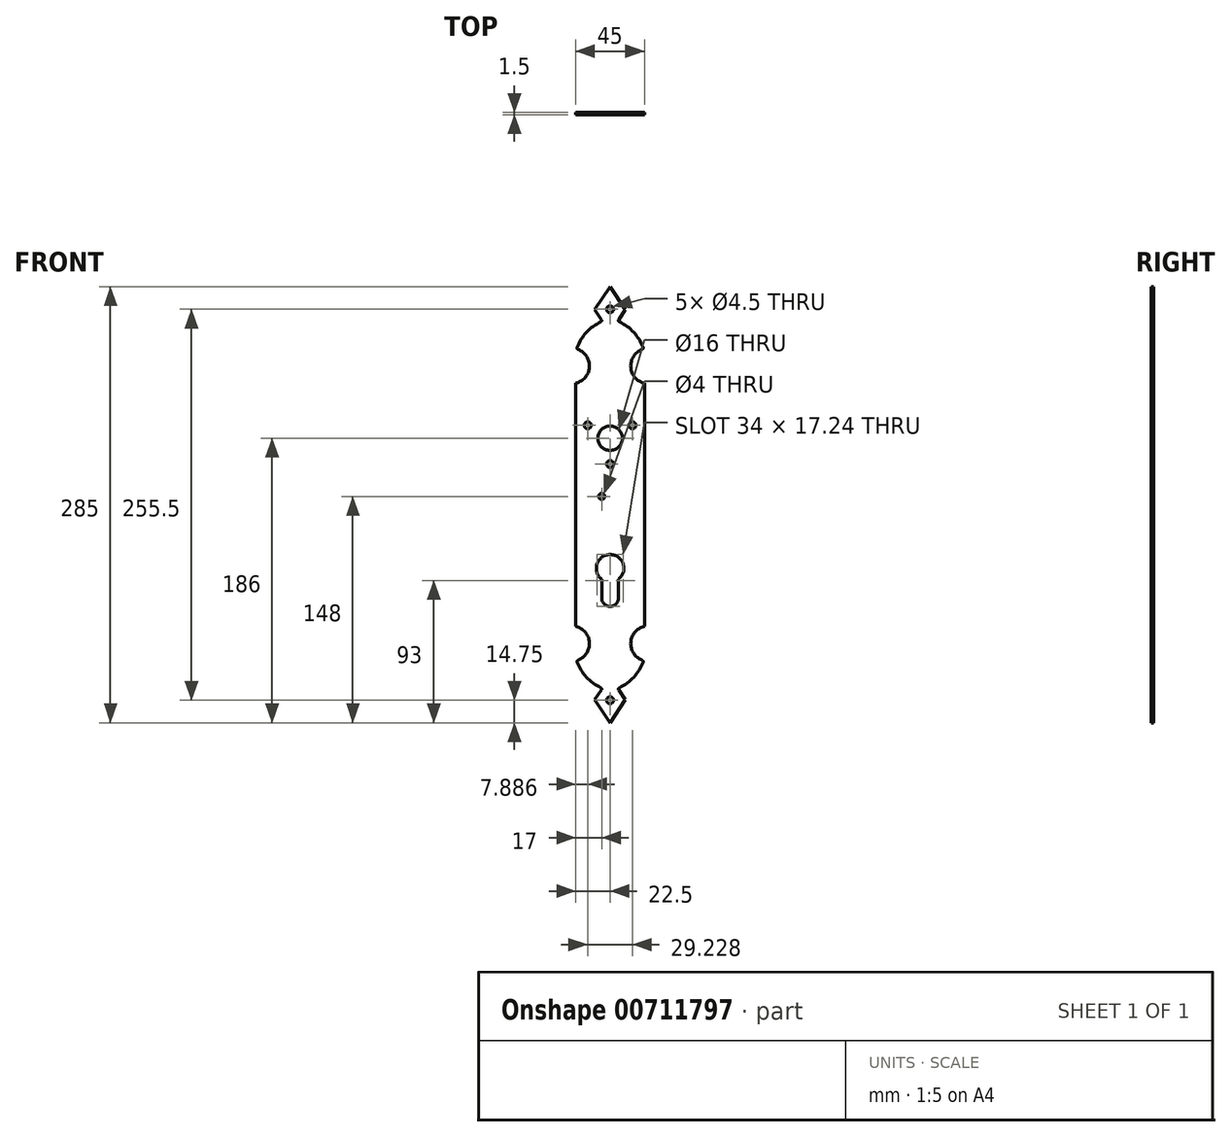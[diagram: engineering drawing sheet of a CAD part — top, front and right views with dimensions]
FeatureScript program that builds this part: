
annotation { "Feature Type Name" : "Feature", "Feature Type Description" : "" }
export const myFeature = defineFeature(function(context is Context, id is Id, definition is map)
    precondition{}
    {
        {
            var Q0;
            Q0=qCreatedBy(makeId("Front.planeOp"),FACE);
            var sketch = newSketch(context, id + "F0", { "sketchPlane" : qUnion([Q0])});
            skLineSegment(sketch, "E0.left", {"start": v(22.5, -79.5) * mm, "end": v(22.5, 79.5) * mm});
            skLineSegment(sketch, "E0.right", {"start": v(-22.5, -79.5) * mm, "end": v(-22.5, 79.5) * mm});
            skPoint(sketch, "E0.middle", {"position": v(0, 0) * mm});
            skLineSegment(sketch, "E1", {"start": v(0, 142.5) * mm, "end": v(-10, 127.5) * mm});
            skLineSegment(sketch, "E2", {"start": v(-10, 127.5) * mm, "end": v(-5.67, 121.06) * mm});
            skArc(sketch, "E3", {"start": v(-6.08, 119.6) * mm, "mid": v(-15.45, 112.71) * mm, "end": v(-21.5, 102.78) * mm});
            skArc(sketch, "E4", {"start": v(-22.5, 79.5) * mm, "mid": v(-13.53, 89.91) * mm, "end": v(-20.92, 101.5) * mm});
            skPoint(sketch, "E5.visualSharp", {"position": v(-5, 120.07) * mm});
            skArc(sketch, "E5.filletArc", {"start": v(-6.08, 119.6) * mm, "mid": v(-5.54, 120.23) * mm, "end": v(-5.67, 121.06) * mm});
            skPoint(sketch, "E6.visualSharp", {"position": v(-21.84, 101.8) * mm});
            skArc(sketch, "E6.filletArc", {"start": v(-21.5, 102.78) * mm, "mid": v(-21.47, 102.02) * mm, "end": v(-20.92, 101.5) * mm});
            skPoint(sketch, "E7.orphan", {"position": v(-22.5, 142.46) * mm});
            skArc(sketch, "E8.MirrorCS", {"start": v(22.5, 79.5) * mm, "mid": v(13.53, 89.91) * mm, "end": v(20.92, 101.5) * mm});
            skArc(sketch, "E9.MirrorCS", {"start": v(21.5, 102.78) * mm, "mid": v(21.47, 102.02) * mm, "end": v(20.92, 101.5) * mm});
            skArc(sketch, "E10.MirrorCS", {"start": v(6.08, 119.6) * mm, "mid": v(15.45, 112.71) * mm, "end": v(21.5, 102.78) * mm});
            skArc(sketch, "E11.MirrorCS", {"start": v(6.08, 119.6) * mm, "mid": v(5.54, 120.23) * mm, "end": v(5.67, 121.06) * mm});
            skLineSegment(sketch, "E12.MirrorCS", {"start": v(0, 142.5) * mm, "end": v(10, 127.5) * mm});
            skLineSegment(sketch, "E13.MirrorCS", {"start": v(10, 127.5) * mm, "end": v(5.67, 121.06) * mm});
            skPoint(sketch, "E14.orphan", {"position": v(22.5, 142.54) * mm});
            skPoint(sketch, "E15.orphan", {"position": v(-23.32, 79.35) * mm});
            skPoint(sketch, "E16.orphan", {"position": v(23.32, 79.35) * mm});
            skPoint(sketch, "E17.orphan", {"position": v(22.5, 93.63) * mm});
            skPoint(sketch, "E18.orphan", {"position": v(-22.5, 93.63) * mm});
            skArc(sketch, "E19.MirrorCS", {"start": v(21.5, -102.78) * mm, "mid": v(21.47, -102.02) * mm, "end": v(20.92, -101.5) * mm});
            skArc(sketch, "E20.MirrorCS", {"start": v(22.5, -79.5) * mm, "mid": v(13.53, -89.91) * mm, "end": v(20.92, -101.5) * mm});
            skArc(sketch, "E21.MirrorCS", {"start": v(6.08, -119.6) * mm, "mid": v(15.45, -112.71) * mm, "end": v(21.5, -102.78) * mm});
            skArc(sketch, "E22.MirrorCS", {"start": v(6.08, -119.6) * mm, "mid": v(5.54, -120.23) * mm, "end": v(5.67, -121.06) * mm});
            skLineSegment(sketch, "E23.MirrorCS", {"start": v(10, -127.5) * mm, "end": v(5.67, -121.06) * mm});
            skLineSegment(sketch, "E24.MirrorCS", {"start": v(0, -142.5) * mm, "end": v(10, -127.5) * mm});
            skLineSegment(sketch, "E25.MirrorCS", {"start": v(-10, -127.5) * mm, "end": v(-5.67, -121.06) * mm});
            skLineSegment(sketch, "E26.MirrorCS", {"start": v(0, -142.5) * mm, "end": v(-10, -127.5) * mm});
            skArc(sketch, "E27.MirrorCS", {"start": v(-6.08, -119.6) * mm, "mid": v(-5.54, -120.23) * mm, "end": v(-5.67, -121.06) * mm});
            skArc(sketch, "E28.MirrorCS", {"start": v(-6.08, -119.6) * mm, "mid": v(-15.45, -112.71) * mm, "end": v(-21.5, -102.78) * mm});
            skArc(sketch, "E29.MirrorCS", {"start": v(-21.5, -102.78) * mm, "mid": v(-21.47, -102.02) * mm, "end": v(-20.92, -101.5) * mm});
            skArc(sketch, "E30.MirrorCS", {"start": v(-22.5, -79.5) * mm, "mid": v(-13.53, -89.91) * mm, "end": v(-20.92, -101.5) * mm});
            skPoint(sketch, "E31.orphan", {"position": v(22.5, -142.46) * mm});
            skPoint(sketch, "E32.orphan", {"position": v(-22.5, -142.54) * mm});
            skPoint(sketch, "E33.orphan", {"position": v(0, 142.5) * mm});
            skCircle(sketch, "E34", {"center": v(0, 127.75) * mm, "radius": 2.25 * mm});
            skCircle(sketch, "E35.MirrorC", {"center": v(0, -127.75) * mm, "radius": 2.25 * mm});
            skCircle(sketch, "E36", {"center": v(0, 43.5) * mm, "radius": 8 * mm});
            skCircle(sketch, "E37", {"center": v(0, 43.5) * mm, "radius": 16.88 * mm, "construction": true});
            skCircle(sketch, "E38", {"center": v(0, 26.63) * mm, "radius": 2.25 * mm});
            skCircle(sketch, "E39", {"center": v(14.61, 51.94) * mm, "radius": 2.25 * mm});
            skCircle(sketch, "E40", {"center": v(-14.61, 51.94) * mm, "radius": 2.25 * mm});
            skLineSegment(sketch, "E41", {"start": v(0, 43.5) * mm, "end": v(-14.61, 51.94) * mm, "construction": true});
            skLineSegment(sketch, "E42", {"start": v(0, 43.5) * mm, "end": v(0, 26.63) * mm, "construction": true});
            skLineSegment(sketch, "E43", {"start": v(0, 43.5) * mm, "end": v(14.61, 51.94) * mm, "construction": true});
            skSolve(sketch);
        }
        {
            var Q0;
            Q0 = qSketchRegion(id + "F0", true);
            extrude(context, id + "F1", {"entities" : qUnion([Q0]), "depth" : 1.5 * mm, "offsetDistance" : 25 * mm});
        }
        {
            var Q0;
            Q0=makeQuery(id+"F1.opExtrude","CAP_FACE",FACE,{"disambiguationData":[OSD([sQuery(id+"F0.wireOp",EDGE,"E0.left"),sQuery(id+"F0.wireOp",EDGE,"E0.right"),sQuery(id+"F0.wireOp",EDGE,"E1"),sQuery(id+"F0.wireOp",EDGE,"E2"),sQuery(id+"F0.wireOp",EDGE,"E3"),sQuery(id+"F0.wireOp",EDGE,"E4"),sQuery(id+"F0.wireOp",EDGE,"E5.filletArc"),sQuery(id+"F0.wireOp",EDGE,"E6.filletArc"),sQuery(id+"F0.wireOp",EDGE,"E8.MirrorCS"),sQuery(id+"F0.wireOp",EDGE,"E9.MirrorCS"),sQuery(id+"F0.wireOp",EDGE,"E10.MirrorCS"),sQuery(id+"F0.wireOp",EDGE,"E11.MirrorCS"),sQuery(id+"F0.wireOp",EDGE,"E12.MirrorCS"),sQuery(id+"F0.wireOp",EDGE,"E13.MirrorCS"),sQuery(id+"F0.wireOp",EDGE,"E19.MirrorCS"),sQuery(id+"F0.wireOp",EDGE,"E20.MirrorCS"),sQuery(id+"F0.wireOp",EDGE,"E21.MirrorCS"),sQuery(id+"F0.wireOp",EDGE,"E22.MirrorCS"),sQuery(id+"F0.wireOp",EDGE,"E23.MirrorCS"),sQuery(id+"F0.wireOp",EDGE,"E24.MirrorCS"),sQuery(id+"F0.wireOp",EDGE,"E25.MirrorCS"),sQuery(id+"F0.wireOp",EDGE,"E26.MirrorCS"),sQuery(id+"F0.wireOp",EDGE,"E27.MirrorCS"),sQuery(id+"F0.wireOp",EDGE,"E28.MirrorCS"),sQuery(id+"F0.wireOp",EDGE,"E29.MirrorCS"),sQuery(id+"F0.wireOp",EDGE,"E30.MirrorCS"),sQuery(id+"F0.wireOp",EDGE,"E34"),sQuery(id+"F0.wireOp",EDGE,"E35.MirrorC")])],"isStart":false});
            var sketch = newSketch(context, id + "F2", { "sketchPlane" : qUnion([Q0])});
            skArc(sketch, "E44", {"start": v(5.5, -48.62) * mm, "mid": v(0, -32.5) * mm, "end": v(-5.5, -48.62) * mm});
            skArc(sketch, "E45", {"start": v(-5.5, -61) * mm, "mid": v(0, -66.5) * mm, "end": v(5.5, -61) * mm});
            skLineSegment(sketch, "E46", {"start": v(5.5, -61) * mm, "end": v(5.5, -48.62) * mm});
            skLineSegment(sketch, "E47", {"start": v(-5.5, -61) * mm, "end": v(-5.5, -48.62) * mm});
            skCircle(sketch, "E48", {"center": v(-5.5, 5.5) * mm, "radius": 2 * mm});
            skSolve(sketch);
        }
        {
            var Q0;
            Q0 = qSketchRegion(id + "F2", true);
            extrude(context, id + "F3", {"entities" : qUnion([Q0]), "operationType" : NewBodyOperationType.REMOVE, "endBound" : BoundingType.UP_TO_NEXT, "oppositeDirection" : true, "depth" : 25 * mm, "offsetDistance" : 25 * mm});
        }
    });
